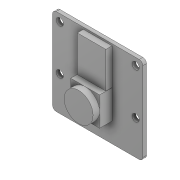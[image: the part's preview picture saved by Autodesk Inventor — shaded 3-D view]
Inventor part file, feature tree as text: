
AUTODESK INVENTOR PART (.ipt)
format: ipt  version: 2020 (Build 240168000, 168)  size: 146,432 bytes
history: mixed  units: mm
features: extrude x3, sketch x3, other x1, imported_body x1
ambient origin geometry x8: Origin, YZ Plane, XZ Plane, XY Plane, X Axis, Y Axis, Z Axis, Center Point
bodies: Solid1 (imported_parasolid)
feature tree (8):
  extrude  "Extrusion1"  Depth=3.0mm TaperAngle=0.0deg
  extrude  "Extrusion3"  [1 undecoded]
  extrude  "Extrusion4"  [1 undecoded]
  sketch  "Sketch1"  dims[d0=19.0mm d1=0.0mm d4=3.0mm d5=0.0mm]
  sketch  "Sketch3"  dims[d6=22.0mm d7=0.0mm]
  sketch  "Sketch4"
  other  "Boss-Extrude1"
  imported_body  NMx_Import_Brep_tag  [imported B-rep: ~28 faces, bbox_mm=[25.0, 24.0, 6.3]]
note: 2 required parameter values undecoded (feature->parameter linkage not recoverable at this tier; creation-order binding heuristic only, values carry confidence <= 0.55)
